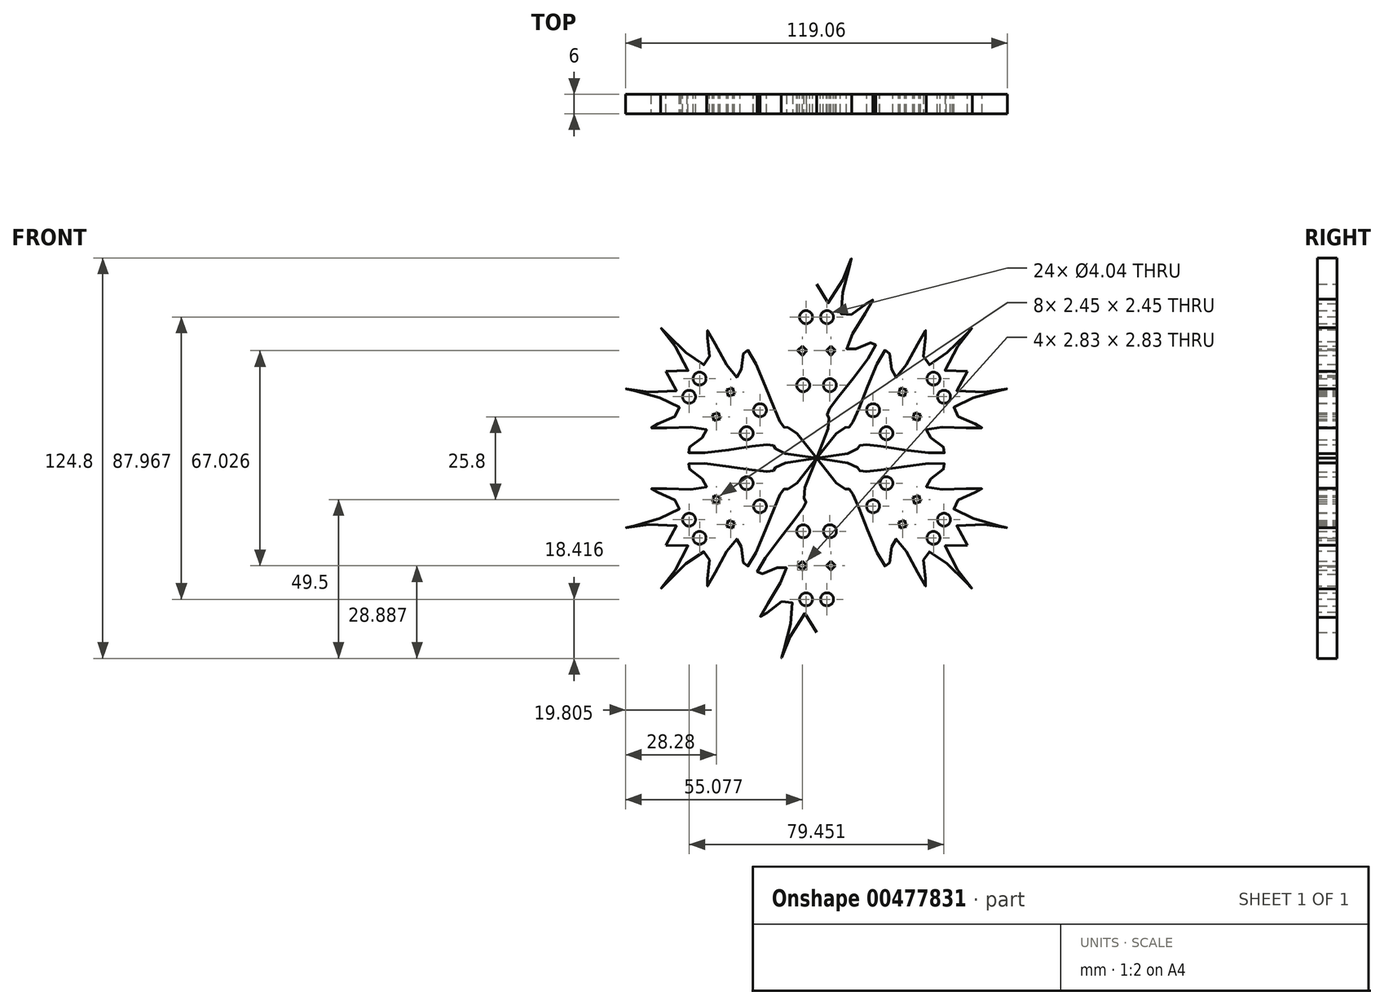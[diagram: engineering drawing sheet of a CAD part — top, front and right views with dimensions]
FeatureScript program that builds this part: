
annotation { "Feature Type Name" : "Feature", "Feature Type Description" : "" }
export const myFeature = defineFeature(function(context is Context, id is Id, definition is map)
    precondition{}
    {
        {
            var Q0;
            Q0=qCreatedBy(makeId("Front.planeOp"),FACE);
            var sketch = newSketch(context, id + "F0", { "sketchPlane" : qUnion([Q0])});
            skLineSegment(sketch, "E0", {"start": v(0, 0) * mm, "end": v(0, 61.65) * mm, "construction": true});
            skFitSpline(sketch, "E1", {"points": [v(0, 54.25) * mm, v(10.75, 61.84) * mm, v(7.93, 44.42) * mm, v(17.5, 49.56) * mm, v(9.47, 33.92) * mm, v(18.17, 36.22) * mm, v(6.61, 18.9) * mm, v(3.3, 13.57) * mm, v(0, 0) * mm], "startDerivative": vector(50.1, -390.34) * mm, "endDerivative": vector(-142.46, -303.97) * mm});
            skCircle(sketch, "E2", {"center": v(3.27, 43.98) * mm, "radius": 2.02 * mm});
            skCircle(sketch, "E3", {"center": v(4.16, 22.76) * mm, "radius": 2.02 * mm});
            skLineSegment(sketch, "E4.bottom", {"start": v(4.45, 34.93) * mm, "end": v(5.87, 33.51) * mm});
            skLineSegment(sketch, "E4.top", {"start": v(3.04, 33.51) * mm, "end": v(4.45, 32.1) * mm});
            skLineSegment(sketch, "E4.left", {"start": v(4.45, 34.93) * mm, "end": v(3.04, 33.51) * mm});
            skLineSegment(sketch, "E4.right", {"start": v(5.87, 33.51) * mm, "end": v(4.45, 32.1) * mm});
            skFitSpline(sketch, "E5.MirrorCS", {"points": [v(0, 54.25) * mm, v(-10.75, 61.84) * mm, v(-7.93, 44.42) * mm, v(-17.5, 49.56) * mm, v(-9.47, 33.92) * mm, v(-18.17, 36.22) * mm, v(-6.61, 18.9) * mm, v(-3.3, 13.57) * mm, v(0, 0) * mm], "startDerivative": vector(-50.1, -390.34) * mm, "endDerivative": vector(142.46, -303.97) * mm});
            skCircle(sketch, "E6.MirrorC", {"center": v(-3.27, 43.98) * mm, "radius": 2.02 * mm});
            skLineSegment(sketch, "E7.MirrorCS", {"start": v(-4.45, 34.93) * mm, "end": v(-3.04, 33.51) * mm});
            skLineSegment(sketch, "E8.MirrorCS", {"start": v(-3.04, 33.51) * mm, "end": v(-4.45, 32.1) * mm});
            skLineSegment(sketch, "E9.MirrorCS", {"start": v(-4.45, 34.93) * mm, "end": v(-5.87, 33.51) * mm});
            skLineSegment(sketch, "E10.MirrorCS", {"start": v(-5.87, 33.51) * mm, "end": v(-4.45, 32.1) * mm});
            skCircle(sketch, "E11.MirrorC", {"center": v(-4.16, 22.76) * mm, "radius": 2.02 * mm});
            skSolve(sketch);
        }
        {
            var Q0;
            Q0 = qSketchRegion(id + "F0", true);
            extrude(context, id + "F1", {"entities" : qUnion([Q0]), "depth" : 6 * mm});
        }
        {
            var Q0;
            Q0=qCreatedBy(makeId("Right.planeOp"),FACE);
            var sketch = newSketch(context, id + "F2", { "sketchPlane" : qUnion([Q0])});
            skLineSegment(sketch, "E12", {"start": v(0, 0) * mm, "end": v(-66.9, 0) * mm, "construction": true});
            skSolve(sketch);
        }
        {
            var Q0;
            Q0=makeQuery(id+"F1.opExtrude","SWEPT_BODY",BODY,{"disambiguationData":[OSD([sQuery(id+"F0.wireOp",EDGE,"E1"),sQuery(id+"F0.wireOp",EDGE,"E2"),sQuery(id+"F0.wireOp",EDGE,"E3"),sQuery(id+"F0.wireOp",EDGE,"E4.bottom"),sQuery(id+"F0.wireOp",EDGE,"E4.top"),sQuery(id+"F0.wireOp",EDGE,"E4.left"),sQuery(id+"F0.wireOp",EDGE,"E4.right"),sQuery(id+"F0.wireOp",EDGE,"E5.MirrorCS"),sQuery(id+"F0.wireOp",EDGE,"E6.MirrorC"),sQuery(id+"F0.wireOp",EDGE,"E7.MirrorCS"),sQuery(id+"F0.wireOp",EDGE,"E8.MirrorCS"),sQuery(id+"F0.wireOp",EDGE,"E9.MirrorCS"),sQuery(id+"F0.wireOp",EDGE,"E10.MirrorCS"),sQuery(id+"F0.wireOp",EDGE,"E11.MirrorC")])]});
            var Q1;
            Q1=sQuery(id+"F2.wireOp",EDGE,"E12");
            circularPattern(context, id + "F3", {"entities" : qUnion([Q0]), "axis" : qUnion([Q1]), "angle" : 360 * degree, "instanceCount" : 6, "equalSpace" : true});
        }
    });
